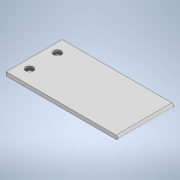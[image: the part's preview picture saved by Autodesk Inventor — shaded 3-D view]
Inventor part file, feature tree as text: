
AUTODESK INVENTOR PART (.ipt)
format: ipt  version: 2020 (Build 240168000, 168)  size: 108,032 bytes
history: native  units: in
note: dims shown in document units (in); Inventor stores cm internally (conversion verified against a paired STEP export)
features: sketch x2, extrude x1, hole x1, fillet x1
ambient origin geometry x8: Origin, YZ Plane, XZ Plane, XY Plane, X Axis, Y Axis, Z Axis, Center Point
bodies: Solid1 (feature_tree)
feature tree (5):
  extrude  "Extrusion1"  Depth=1.5in
  hole  "Hole1"  [1 undecoded]
  fillet  "Fillet1"  Radius=0.375in
  sketch  "Sketch1"  dims[d0=3.0in d1=1.5in]
  sketch  "Sketch2"  dims[d2=0.1in d3=0.0in d4=0.25in d5=0.375in d6=0.375in d7=0.2in d8=0.75in d9=0.375in d10=0.25in d11=0.5635in d12=0.5in d13=0.8108in d14=0.05in]
note: 1 required parameter value undecoded (feature->parameter linkage not recoverable at this tier; creation-order binding heuristic only, values carry confidence <= 0.55)
